# Revit family: Domotics-DomesticRanges-GEWISS-SYSTEM_SIGNALLING-LAMP_STAIR_RISER_2M
name_source: partatom
category: Apparecchi elettrici
revit_build: Autodesk Revit 2016 (Build: 20161004_0715(x64)
units: mm (PartAtom-declared; Revit-internal decimal feet)

## family parameters
Condiviso = Sì
Host = Superficie
Mantenere orientamento annotazione = Sì
Punto di calcolo locali = Sì
Quota connettore circolare = Usa diametro
Taglio con vuoti quando caricato = Sì
Tipo di parte = Normale

## types (2) — shared parameters
Carico apparente = 0 VA
Catalogue = DOMOTICS
Catalogue Range = SYSTEM - DOMESTIC RANGE
Description. = Stair riser lamp
Diffuser colour = White
Diffuser colour: = White
Electrocod = 0132
IDF = e1f8d91e-42d5-45ae-9b50-bb8d477e07d2
IDT = 4cbe2d01-671d-42f3-b0a9-0d3cd50f0d86
Immagine tipo = GW21634.jpg
Lamp = Integrated LED
Lamp voltage = 12V ac/dc - 230V ac
N. poli = 1
No. SYSTEM modules = 2
Produttore = GEWISS S.p.A.
Prospetto di default = 1219 mm
SEO = Lamp
Technical sheet = https://www.gewiss.com
Tipo = System Spie Segnapasso 2M_GENERICO : GW21634 Spia segnapasso 12/230V 2M nero
Type of lamp = Integrated LED
URL = https://www.gewiss.com
Version file RFA = 19.4
Volt = 230 V
Voltage = 12/230V AC
Voltage: = 12/230V AC

## per-type parameters (varying)
| type | Colour | Descrizione | EAN code | Modello |
| GW20634 - Stair riser lamp 12/230V 2M white | White | STAIR RISER LAMP 12/230V 2M SY/WT | 8011564184664 | GW20634 |
| GW21634 - Stair riser lamp 12/230V 2M black | Black | STAIR RISER LAMP 12/230V 2M SY/BK | 8011564184671 | GW21634 |

## geometry (parser evidence)
native form markers: Blend x4, Sweep x2
no freeform markers — native parametric forms only
